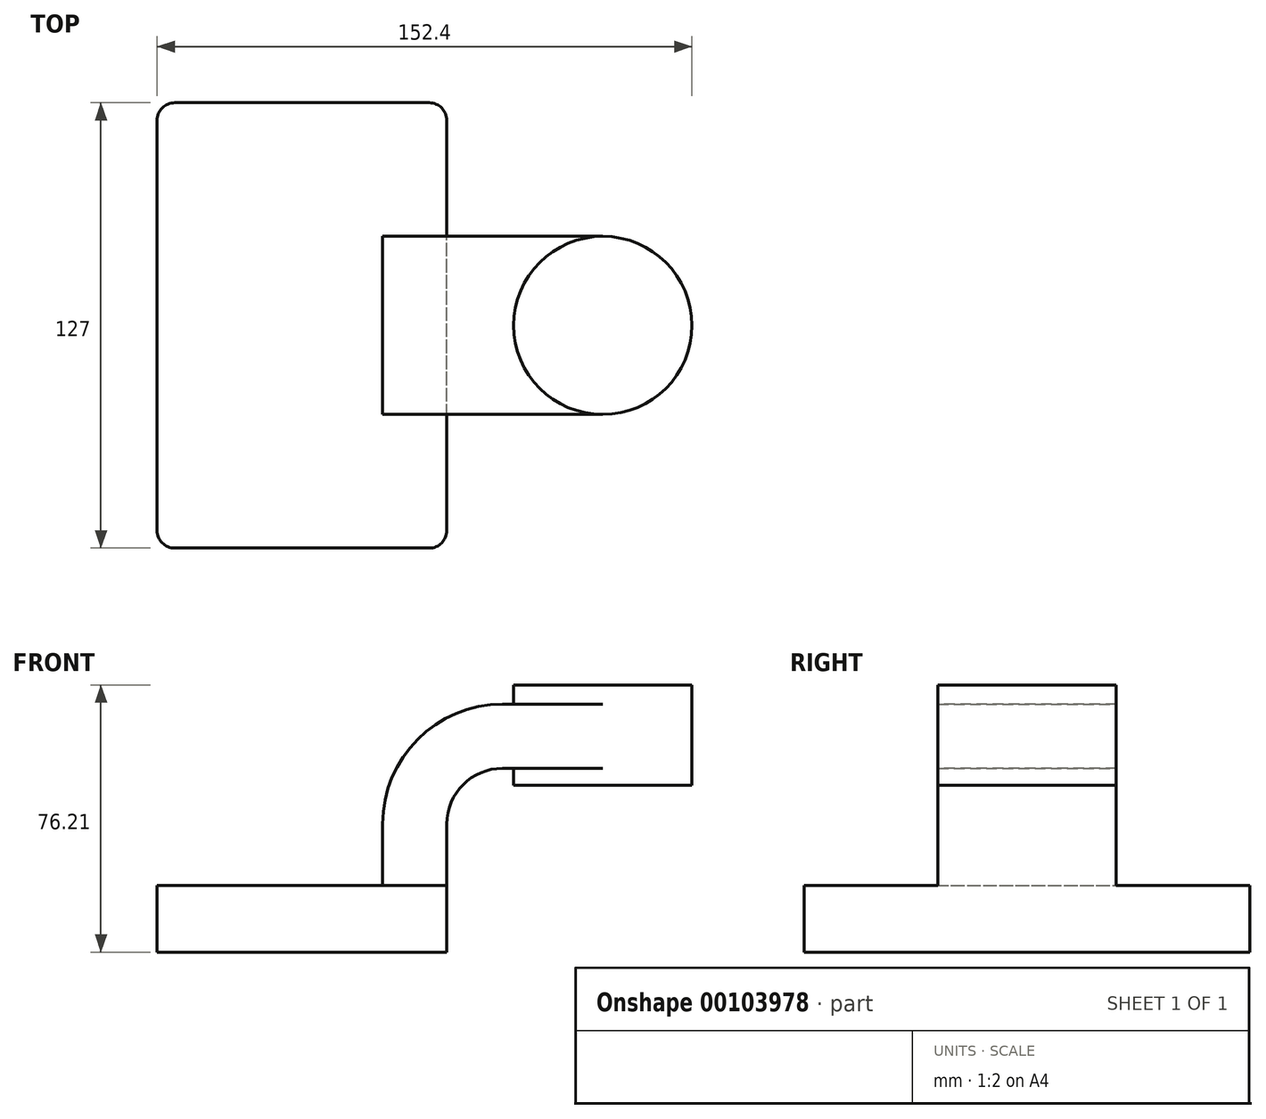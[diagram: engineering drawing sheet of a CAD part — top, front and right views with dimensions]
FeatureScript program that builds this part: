
annotation { "Feature Type Name" : "Feature", "Feature Type Description" : "" }
export const myFeature = defineFeature(function(context is Context, id is Id, definition is map)
    precondition{}
    {
        {
            var Q0;
            Q0=qCreatedBy(makeId("Front.planeOp"),FACE);
            var sketch = newSketch(context, id + "F0", { "sketchPlane" : qUnion([Q0])});
            skLineSegment(sketch, "E0.bottom", {"start": v(-41.28, 9.52) * mm, "end": v(41.28, 9.53) * mm});
            skLineSegment(sketch, "E0.top", {"start": v(-41.28, -9.53) * mm, "end": v(41.28, -9.53) * mm});
            skLineSegment(sketch, "E0.left", {"start": v(-41.27, 9.52) * mm, "end": v(-41.27, -9.53) * mm});
            skLineSegment(sketch, "E0.right", {"start": v(41.28, 9.53) * mm, "end": v(41.28, -9.52) * mm});
            skPoint(sketch, "E0.middle", {"position": v(0, 0) * mm});
            skLineSegment(sketch, "E1.bottom", {"start": v(111.12, 38.1) * mm, "end": v(60.32, 38.1) * mm});
            skLineSegment(sketch, "E1.top", {"start": v(111.12, 66.68) * mm, "end": v(60.32, 66.68) * mm});
            skLineSegment(sketch, "E1.left", {"start": v(111.12, 38.1) * mm, "end": v(111.12, 66.67) * mm});
            skLineSegment(sketch, "E1.right", {"start": v(60.32, 38.1) * mm, "end": v(60.32, 66.67) * mm});
            skPoint(sketch, "E1.middle", {"position": v(85.72, 52.39) * mm});
            skLineSegment(sketch, "E2", {"start": v(41.28, 9.53) * mm, "end": v(41.28, 27) * mm});
            skArc(sketch, "E3", {"start": v(41.27, 27) * mm, "mid": v(45.92, 38.23) * mm, "end": v(57.15, 42.88) * mm});
            skLineSegment(sketch, "E4", {"start": v(57.15, 42.88) * mm, "end": v(85.72, 42.88) * mm});
            skLineSegment(sketch, "E5.0", {"start": v(57.15, 61.15) * mm, "end": v(85.72, 61.15) * mm});
            skArc(sketch, "E5.1", {"start": v(23, 27) * mm, "mid": v(33, 51.15) * mm, "end": v(57.15, 61.15) * mm});
            skLineSegment(sketch, "E5.2", {"start": v(23, 9.53) * mm, "end": v(23, 27) * mm});
            skLineSegment(sketch, "E6", {"start": v(85.72, 66.68) * mm, "end": v(85.72, 38.1) * mm});
            skFitSpline(sketch, "E7", {"points": [v(57.15, 61.15) * mm, v(-41.28, 9.52) * mm], "startDerivative": vector(-140.6, 0) * mm, "endDerivative": vector(0, -111.14) * mm});
            skSolve(sketch);
        }
        {
            var Q0;
            Q0=makeQuery(id+"F0.imprint","IMPRINT",FACE,{"disambiguationData":[TD([[makeQuery(id+"F0.imprint","IMPRINT",EDGE,{"derivedFrom":sQuery(id+"F0.wireOp",EDGE,"E0.top")}),1.0]])]});
            extrude(context, id + "F1", {"entities" : qUnion([Q0]), "endBound" : BoundingType.SYMMETRIC, "depth" : 127 * mm});
        }
        {
            var Q0;
            {var subQ1=sQuery(id+"F0.wireOp",EDGE,"E2");Q0=makeQuery(id+"F0.imprint","IMPRINT",FACE,{"disambiguationData":[TD([[makeQuery(id+"F0.imprint","IMPRINT",EDGE,{"derivedFrom":subQ1}),1.0]])]});}
            var Q1;
            {var subQ0=sQuery(id+"F0.wireOp",EDGE,"E4");var subQ1=sQuery(id+"F0.wireOp",EDGE,"E1.right");var subQ2=makeQuery(id+"F0.imprint","INTERSECT",VERTEX,{"derivedFrom":[subQ1,subQ0]});Q1=makeQuery(id+"F0.imprint","IMPRINT",FACE,{"disambiguationData":[TD([[makeQuery(id+"F0.imprint","IMPRINT",EDGE,{"disambiguationData":[TD([[subQ2,-1.0]])],"derivedFrom":subQ1}),-1.0]])]});}
            extrude(context, id + "F2", {"entities" : qUnion([Q0, Q1]), "operationType" : NewBodyOperationType.ADD, "endBound" : BoundingType.SYMMETRIC, "depth" : 50.8 * mm});
        }
        {
            var Q0;
            Q0=makeQuery(id+"F0.imprint","IMPRINT",FACE,{"disambiguationData":[TD([[makeQuery(id+"F0.imprint","IMPRINT",EDGE,{"derivedFrom":sQuery(id+"F0.wireOp",EDGE,"E5.1")}),1.0]])]});
            extrude(context, id + "F3", {"entities" : qUnion([Q0]), "operationType" : NewBodyOperationType.ADD, "endBound" : BoundingType.SYMMETRIC, "depth" : 25 * mm});
        }
        {
            var Q0;
            {var subQ0=sQuery(id+"F0.wireOp",EDGE,"E1.left");Q0=makeQuery(id+"F0.imprint","IMPRINT",FACE,{"disambiguationData":[TD([[makeQuery(id+"F0.imprint","IMPRINT",EDGE,{"derivedFrom":subQ0}),1.0]])]});}
            var Q1;
            Q1=sQuery(id+"F0.wireOp",EDGE,"E6");
            revolve(context, id + "F4", {"operationType" : NewBodyOperationType.ADD, "entities" : qUnion([Q0]), "axis" : qUnion([Q1]), "revolveType" : RevolveType.FULL});
        }
        {
            var Q0;
            Q0=makeQuery(id+"F1.opExtrude","CAP_EDGE",EDGE,{"disambiguationData":[OSD([sQuery(id+"F0.wireOp",EDGE,"E0.right")])],"isStart":false});
            var Q1;
            Q1=makeQuery(id+"F1.opExtrude","CAP_EDGE",EDGE,{"disambiguationData":[OSD([sQuery(id+"F0.wireOp",EDGE,"E0.left")])],"isStart":false});
            var Q2;
            Q2=makeQuery(id+"F1.opExtrude","CAP_EDGE",EDGE,{"disambiguationData":[OSD([sQuery(id+"F0.wireOp",EDGE,"E0.right")])],"isStart":true});
            var Q3;
            Q3=makeQuery(id+"F1.opExtrude","CAP_EDGE",EDGE,{"disambiguationData":[OSD([sQuery(id+"F0.wireOp",EDGE,"E0.left")])],"isStart":true});
            fillet(context, id + "F5", {"entities" : qUnion([Q0, Q1, Q2, Q3]), "radius" : 5 * mm, "tangentPropagation" : true, "allowEdgeOverflow" : false});
        }
    });
